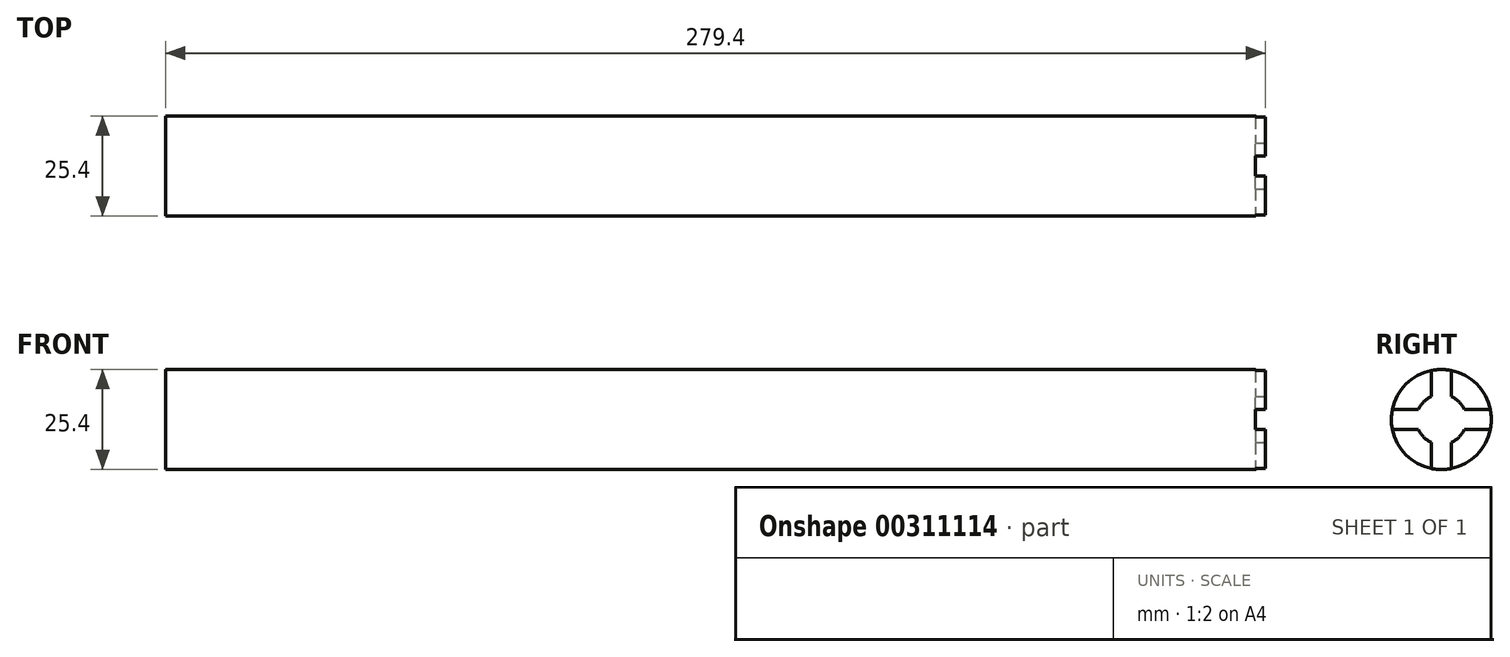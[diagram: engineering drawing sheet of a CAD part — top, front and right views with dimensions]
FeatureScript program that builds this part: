
annotation { "Feature Type Name" : "Feature", "Feature Type Description" : "" }
export const myFeature = defineFeature(function(context is Context, id is Id, definition is map)
    precondition{}
    {
        {
            var Q0;
            Q0=qCreatedBy(makeId("Right.planeOp"),FACE);
            var sketch = newSketch(context, id + "F0", { "sketchPlane" : qUnion([Q0])});
            skLineSegment(sketch, "E0", {"start": v(0, 0) * mm, "end": v(25.4, 0) * mm});
            skLineSegment(sketch, "E1", {"start": v(25.4, 0) * mm, "end": v(25.4, 25.4) * mm});
            skLineSegment(sketch, "E2", {"start": v(25.4, 25.4) * mm, "end": v(0, 25.4) * mm});
            skLineSegment(sketch, "E3", {"start": v(0, 25.4) * mm, "end": v(0, 0) * mm});
            skSolve(sketch);
        }
        {
            var Q0;
            Q0 = qSketchRegion(id + "F0", true);
            extrude(context, id + "F1", {"entities" : qUnion([Q0]), "depth" : 279.4 * mm});
        }
        {
            var Q0;
            Q0=makeQuery(id+"F1.opExtrude","CAP_FACE",FACE,{"disambiguationData":[OSD([sQuery(id+"F0.wireOp",EDGE,"E0"),sQuery(id+"F0.wireOp",EDGE,"E1"),sQuery(id+"F0.wireOp",EDGE,"E2"),sQuery(id+"F0.wireOp",EDGE,"E3")])],"isStart":false});
            var sketch = newSketch(context, id + "F2", { "sketchPlane" : qUnion([Q0])});
            skLineSegment(sketch, "E4", {"start": v(12.7, 25.4) * mm, "end": v(12.7, 12.7) * mm});
            skCircle(sketch, "E5", {"center": v(12.7, 12.7) * mm, "radius": 6.35 * mm});
            skLineSegment(sketch, "E6", {"start": v(25.4, 15.24) * mm, "end": v(18.52, 15.24) * mm});
            skLineSegment(sketch, "E7", {"start": v(25.4, 10.16) * mm, "end": v(18.52, 10.16) * mm});
            skLineSegment(sketch, "E8", {"start": v(25.4, 10.16) * mm, "end": v(25.4, 15.24) * mm});
            skLineSegment(sketch, "E9", {"start": v(25.4, 0) * mm, "end": v(15.24, 0) * mm});
            skLineSegment(sketch, "E10", {"start": v(15.24, 6.88) * mm, "end": v(10.16, 6.88) * mm});
            skLineSegment(sketch, "E11", {"start": v(10.16, 6.88) * mm, "end": v(10.16, 0) * mm});
            skLineSegment(sketch, "E12", {"start": v(6.88, 10.16) * mm, "end": v(0, 10.16) * mm});
            skLineSegment(sketch, "E13", {"start": v(6.88, 15.24) * mm, "end": v(0, 15.24) * mm});
            skLineSegment(sketch, "E14", {"start": v(0, 25.4) * mm, "end": v(10.16, 25.4) * mm});
            skLineSegment(sketch, "E15", {"start": v(10.16, 18.52) * mm, "end": v(10.16, 25.4) * mm});
            skLineSegment(sketch, "E16", {"start": v(15.24, 0) * mm, "end": v(15.24, 6.88) * mm});
            skLineSegment(sketch, "E17", {"start": v(15.24, 0) * mm, "end": v(10.16, 0) * mm});
            skLineSegment(sketch, "E18", {"start": v(15.24, 25.4) * mm, "end": v(10.16, 25.4) * mm});
            skLineSegment(sketch, "E19", {"start": v(15.24, 25.4) * mm, "end": v(15.24, 18.52) * mm});
            skLineSegment(sketch, "E20", {"start": v(15.24, 18.52) * mm, "end": v(10.16, 18.52) * mm});
            skLineSegment(sketch, "E21", {"start": v(0, 15.24) * mm, "end": v(0, 10.16) * mm});
            skLineSegment(sketch, "E22", {"start": v(10.16, 0) * mm, "end": v(15.24, 0) * mm});
            skSolve(sketch);
        }
        {
            var Q0;
            Q0 = qSketchRegion(id + "F2", true);
            extrude(context, id + "F3", {"entities" : qUnion([Q0]), "operationType" : NewBodyOperationType.REMOVE, "oppositeDirection" : true, "depth" : 2.54 * mm});
        }
        {
            var Q0;
            Q0=makeQuery(id+"F1.opExtrude","SWEPT_EDGE",EDGE,{"disambiguationData":[OSD([sQuery(id+"F0.wireOp",EDGE,"E1"),sQuery(id+"F0.wireOp",EDGE,"E2")])]});
            var Q1;
            Q1=makeQuery(id+"F1.opExtrude","SWEPT_EDGE",EDGE,{"disambiguationData":[OSD([sQuery(id+"F0.wireOp",EDGE,"E0"),sQuery(id+"F0.wireOp",EDGE,"E1")])]});
            var Q2;
            Q2=makeQuery(id+"F1.opExtrude","SWEPT_EDGE",EDGE,{"disambiguationData":[OSD([sQuery(id+"F0.wireOp",EDGE,"E2"),sQuery(id+"F0.wireOp",EDGE,"E3")])]});
            var Q3;
            Q3=makeQuery(id+"F1.opExtrude","SWEPT_EDGE",EDGE,{"disambiguationData":[OSD([sQuery(id+"F0.wireOp",EDGE,"E0"),sQuery(id+"F0.wireOp",EDGE,"E3")])]});
            fillet(context, id + "F4", {"entities" : qUnion([Q0, Q1, Q2, Q3]), "radius" : 12.7 * mm, "tangentPropagation" : true, "allowEdgeOverflow" : false});
        }
    });
